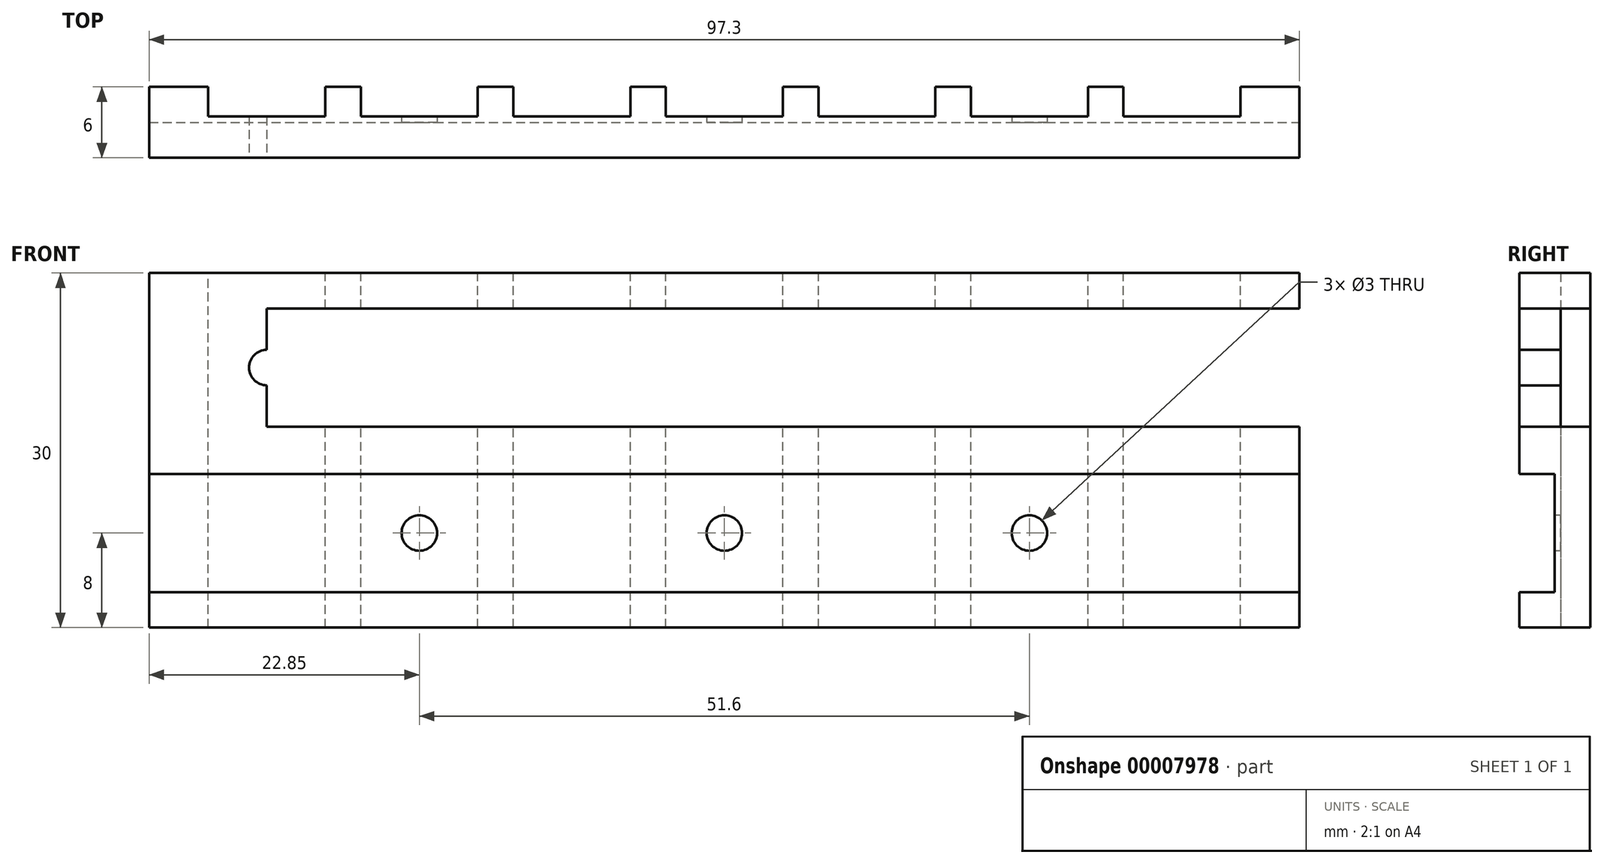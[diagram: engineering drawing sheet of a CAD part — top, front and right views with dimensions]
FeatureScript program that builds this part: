
annotation { "Feature Type Name" : "Feature", "Feature Type Description" : "" }
export const myFeature = defineFeature(function(context is Context, id is Id, definition is map)
    precondition{}
    {
        {
            var Q0;
            Q0=qCreatedBy(makeId("Front.planeOp"),FACE);
            var sketch = newSketch(context, id + "F0", { "sketchPlane" : qUnion([Q0])});
            skLineSegment(sketch, "E0.bottom", {"start": v(0, 0) * mm, "end": v(97.3, 0) * mm});
            skLineSegment(sketch, "E0.top", {"start": v(0, 30) * mm, "end": v(97.3, 30) * mm});
            skLineSegment(sketch, "E0.left", {"start": v(0, 0) * mm, "end": v(0, 30) * mm});
            skLineSegment(sketch, "E0.right", {"start": v(97.3, 0) * mm, "end": v(97.3, 30) * mm});
            skLineSegment(sketch, "E1.bottom", {"start": v(0, 27) * mm, "end": v(97.3, 27) * mm});
            skLineSegment(sketch, "E1.top", {"start": v(0, 17) * mm, "end": v(97.3, 17) * mm});
            skLineSegment(sketch, "E1.left", {"start": v(0, 27) * mm, "end": v(0, 17) * mm});
            skLineSegment(sketch, "E1.right", {"start": v(97.3, 27) * mm, "end": v(97.3, 17) * mm});
            skLineSegment(sketch, "E2.bottom", {"start": v(0, 13) * mm, "end": v(97.3, 13) * mm});
            skLineSegment(sketch, "E2.top", {"start": v(0, 3) * mm, "end": v(97.3, 3) * mm});
            skLineSegment(sketch, "E2.left", {"start": v(0, 13) * mm, "end": v(0, 3) * mm});
            skLineSegment(sketch, "E2.right", {"start": v(97.3, 13) * mm, "end": v(97.3, 3) * mm});
            skPoint(sketch, "E3.1", {"position": v(9.95, 0) * mm});
            skLineSegment(sketch, "E4", {"start": v(9.95, 0) * mm, "end": v(9.95, 30) * mm, "construction": true});
            skLineSegment(sketch, "E5", {"start": v(9.95, 27) * mm, "end": v(9.95, 17) * mm});
            skPoint(sketch, "E6", {"position": v(9.95, 22) * mm});
            skCircle(sketch, "E7", {"center": v(9.95, 22) * mm, "radius": 1.5 * mm});
            skCircle(sketch, "E8.1.0.0", {"center": v(35.75, 22) * mm, "radius": 1.5 * mm});
            skCircle(sketch, "E8.2.0.0", {"center": v(61.55, 22) * mm, "radius": 1.5 * mm});
            skCircle(sketch, "E8.3.0.0", {"center": v(87.35, 22) * mm, "radius": 1.5 * mm});
            skLineSegment(sketch, "E8.direction1", {"start": v(9.95, 22) * mm, "end": v(35.75, 22) * mm, "construction": true});
            skLineSegment(sketch, "E9.1.0.0", {"start": v(22.85, 0) * mm, "end": v(22.85, 30) * mm, "construction": true});
            skLineSegment(sketch, "E9.2.0.0", {"start": v(35.75, 0) * mm, "end": v(35.75, 30) * mm, "construction": true});
            skLineSegment(sketch, "E9.3.0.0", {"start": v(48.65, 0) * mm, "end": v(48.65, 30) * mm, "construction": true});
            skLineSegment(sketch, "E9.4.0.0", {"start": v(61.55, 0) * mm, "end": v(61.55, 30) * mm, "construction": true});
            skLineSegment(sketch, "E9.5.0.0", {"start": v(74.45, 0) * mm, "end": v(74.45, 30) * mm, "construction": true});
            skLineSegment(sketch, "E9.6.0.0", {"start": v(87.35, 0) * mm, "end": v(87.35, 30) * mm, "construction": true});
            skLineSegment(sketch, "E9.direction1", {"start": v(9.95, 0) * mm, "end": v(22.85, 0) * mm, "construction": true});
            skPoint(sketch, "E10", {"position": v(9.95, 8) * mm});
            skPoint(sketch, "E10.positionSnap0", {"position": v(0, 8) * mm});
            skLineSegment(sketch, "E11", {"start": v(0, 8) * mm, "end": v(97.3, 8) * mm, "construction": true});
            skCircle(sketch, "E12", {"center": v(22.85, 8) * mm, "radius": 1.5 * mm});
            skCircle(sketch, "E13.1.0.0", {"center": v(48.65, 8) * mm, "radius": 1.5 * mm});
            skCircle(sketch, "E13.2.0.0", {"center": v(74.45, 8) * mm, "radius": 1.5 * mm});
            skLineSegment(sketch, "E13.direction1", {"start": v(22.85, 8) * mm, "end": v(48.65, 8) * mm, "construction": true});
            skSolve(sketch);
        }
        {
            var Q0;
            Q0=makeQuery(id+"F0.imprint","IMPRINT",FACE,{"disambiguationData":[TD([[makeQuery(id+"F0.imprint","IMPRINT",EDGE,{"derivedFrom":sQuery(id+"F0.wireOp",EDGE,"E1.bottom")}),-1.0]])]});
            var Q1;
            {var subQ0=sQuery(id+"F0.wireOp",EDGE,"E1.top");Q1=makeQuery(id+"F0.imprint","IMPRINT",FACE,{"disambiguationData":[TD([[makeQuery(id+"F0.imprint","IMPRINT",EDGE,{"derivedFrom":subQ0}),-1.0]])]});}
            var Q2;
            Q2=makeQuery(id+"F0.imprint","IMPRINT",FACE,{"disambiguationData":[TD([[makeQuery(id+"F0.imprint","IMPRINT",EDGE,{"derivedFrom":sQuery(id+"F0.wireOp",EDGE,"E2.bottom")}),-1.0]])]});
            var Q3;
            {var subQ0=sQuery(id+"F0.wireOp",EDGE,"E0.bottom");Q3=makeQuery(id+"F0.imprint","IMPRINT",FACE,{"disambiguationData":[TD([[makeQuery(id+"F0.imprint","IMPRINT",EDGE,{"derivedFrom":subQ0}),1.0]])]});}
            var Q4;
            {var subQ8=sQuery(id+"F0.wireOp",EDGE,"E2.bottom");Q4=makeQuery(id+"F0.imprint","IMPRINT",FACE,{"disambiguationData":[TD([[makeQuery(id+"F0.imprint","IMPRINT",EDGE,{"derivedFrom":subQ8}),1.0]])]});}
            var Q5;
            {var subQ0=sQuery(id+"F0.wireOp",EDGE,"E1.bottom");var subQ1=makeQuery(id+"F0.imprint","INTERSECT",VERTEX,{"derivedFrom":[subQ0,sQuery(id+"F0.wireOp",EDGE,"E5")]});Q5=makeQuery(id+"F0.imprint","IMPRINT",FACE,{"disambiguationData":[TD([[makeQuery(id+"F0.imprint","IMPRINT",EDGE,{"disambiguationData":[TD([[subQ1,1.0]])],"derivedFrom":subQ0}),1.0]])]});}
            var Q6;
            {var subQ0=sQuery(id+"F0.wireOp",EDGE,"E1.top");var subQ1=makeQuery(id+"F0.imprint","INTERSECT",VERTEX,{"derivedFrom":[subQ0,sQuery(id+"F0.wireOp",EDGE,"E5")]});Q6=makeQuery(id+"F0.imprint","IMPRINT",FACE,{"disambiguationData":[TD([[makeQuery(id+"F0.imprint","IMPRINT",EDGE,{"disambiguationData":[TD([[subQ1,1.0]])],"derivedFrom":subQ0}),-1.0]])]});}
            var Q7;
            {var subQ0=sQuery(id+"F0.wireOp",EDGE,"E8.1.0.0");var subQ1=sQuery(id+"F0.wireOp",EDGE,"E1.top");var subQ2=makeQuery(id+"F0.imprint","INTERSECT",VERTEX,{"disambiguationData":[OD(0.0)],"derivedFrom":[subQ1,subQ0]});Q7=makeQuery(id+"F0.imprint","IMPRINT",FACE,{"disambiguationData":[TD([[makeQuery(id+"F0.imprint","IMPRINT",EDGE,{"disambiguationData":[TD([[subQ2,-1.0]])],"derivedFrom":subQ1}),-1.0]])]});}
            var Q8;
            {var subQ0=sQuery(id+"F0.wireOp",EDGE,"E8.2.0.0");var subQ1=sQuery(id+"F0.wireOp",EDGE,"E1.top");var subQ2=makeQuery(id+"F0.imprint","INTERSECT",VERTEX,{"disambiguationData":[OD(0.0)],"derivedFrom":[subQ1,subQ0]});Q8=makeQuery(id+"F0.imprint","IMPRINT",FACE,{"disambiguationData":[TD([[makeQuery(id+"F0.imprint","IMPRINT",EDGE,{"disambiguationData":[TD([[subQ2,-1.0]])],"derivedFrom":subQ1}),-1.0]])]});}
            var Q9;
            {var subQ0=sQuery(id+"F0.wireOp",EDGE,"E8.3.0.0");var subQ1=sQuery(id+"F0.wireOp",EDGE,"E1.top");var subQ2=makeQuery(id+"F0.imprint","INTERSECT",VERTEX,{"disambiguationData":[OD(0.0)],"derivedFrom":[subQ1,subQ0]});Q9=makeQuery(id+"F0.imprint","IMPRINT",FACE,{"disambiguationData":[TD([[makeQuery(id+"F0.imprint","IMPRINT",EDGE,{"disambiguationData":[TD([[subQ2,-1.0]])],"derivedFrom":subQ1}),-1.0]])]});}
            var Q10;
            {var subQ17=sQuery(id+"F0.wireOp",EDGE,"E0.top");Q10=makeQuery(id+"F0.imprint","IMPRINT",FACE,{"disambiguationData":[TD([[makeQuery(id+"F0.imprint","IMPRINT",EDGE,{"derivedFrom":subQ17}),-1.0]])]});}
            var Q11;
            {var subQ0=sQuery(id+"F0.wireOp",EDGE,"E8.1.0.0");var subQ1=sQuery(id+"F0.wireOp",EDGE,"E1.bottom");var subQ2=makeQuery(id+"F0.imprint","INTERSECT",VERTEX,{"disambiguationData":[OD(0.0)],"derivedFrom":[subQ1,subQ0]});Q11=makeQuery(id+"F0.imprint","IMPRINT",FACE,{"disambiguationData":[TD([[makeQuery(id+"F0.imprint","IMPRINT",EDGE,{"disambiguationData":[TD([[subQ2,-1.0]])],"derivedFrom":subQ1}),1.0]])]});}
            var Q12;
            {var subQ0=sQuery(id+"F0.wireOp",EDGE,"E8.2.0.0");var subQ1=sQuery(id+"F0.wireOp",EDGE,"E1.bottom");var subQ2=makeQuery(id+"F0.imprint","INTERSECT",VERTEX,{"disambiguationData":[OD(0.0)],"derivedFrom":[subQ1,subQ0]});Q12=makeQuery(id+"F0.imprint","IMPRINT",FACE,{"disambiguationData":[TD([[makeQuery(id+"F0.imprint","IMPRINT",EDGE,{"disambiguationData":[TD([[subQ2,-1.0]])],"derivedFrom":subQ1}),1.0]])]});}
            var Q13;
            {var subQ0=sQuery(id+"F0.wireOp",EDGE,"E8.3.0.0");var subQ1=sQuery(id+"F0.wireOp",EDGE,"E1.bottom");var subQ2=makeQuery(id+"F0.imprint","INTERSECT",VERTEX,{"disambiguationData":[OD(0.0)],"derivedFrom":[subQ1,subQ0]});Q13=makeQuery(id+"F0.imprint","IMPRINT",FACE,{"disambiguationData":[TD([[makeQuery(id+"F0.imprint","IMPRINT",EDGE,{"disambiguationData":[TD([[subQ2,-1.0]])],"derivedFrom":subQ1}),1.0]])]});}
            var Q14;
            {var subQ5=sQuery(id+"F0.wireOp",EDGE,"E1.right");Q14=makeQuery(id+"F0.imprint","IMPRINT",FACE,{"disambiguationData":[TD([[makeQuery(id+"F0.imprint","IMPRINT",EDGE,{"derivedFrom":subQ5}),-1.0]])]});}
            extrude(context, id + "F1", {"entities" : qUnion([Q0, Q1, Q2, Q3, Q4, Q5, Q6, Q7, Q8, Q9, Q10, Q11, Q12, Q13, Q14]), "oppositeDirection" : true, "depth" : 6 * mm});
        }
        {
            var Q0;
            Q0=qCreatedBy(makeId("Top.planeOp"),FACE);
            var sketch = newSketch(context, id + "F2", { "sketchPlane" : qUnion([Q0])});
            skLineSegment(sketch, "E14.bottom", {"start": v(5, 13.4) * mm, "end": v(14.9, 13.4) * mm});
            skLineSegment(sketch, "E14.top", {"start": v(5, 3.5) * mm, "end": v(14.9, 3.5) * mm});
            skLineSegment(sketch, "E14.left", {"start": v(5, 13.4) * mm, "end": v(5, 3.5) * mm});
            skLineSegment(sketch, "E14.right", {"start": v(14.9, 13.4) * mm, "end": v(14.9, 3.5) * mm});
            skLineSegment(sketch, "E15.1.0.0", {"start": v(27.8, 13.4) * mm, "end": v(27.8, 3.5) * mm});
            skLineSegment(sketch, "E15.1.0.1", {"start": v(17.9, 3.5) * mm, "end": v(27.8, 3.5) * mm});
            skLineSegment(sketch, "E15.1.0.2", {"start": v(17.9, 13.4) * mm, "end": v(17.9, 3.5) * mm});
            skLineSegment(sketch, "E15.1.0.3", {"start": v(17.9, 13.4) * mm, "end": v(27.8, 13.4) * mm});
            skLineSegment(sketch, "E15.2.0.0", {"start": v(40.7, 13.4) * mm, "end": v(40.7, 3.5) * mm});
            skLineSegment(sketch, "E15.2.0.1", {"start": v(30.8, 3.5) * mm, "end": v(40.7, 3.5) * mm});
            skLineSegment(sketch, "E15.2.0.2", {"start": v(30.8, 13.4) * mm, "end": v(30.8, 3.5) * mm});
            skLineSegment(sketch, "E15.2.0.3", {"start": v(30.8, 13.4) * mm, "end": v(40.7, 13.4) * mm});
            skLineSegment(sketch, "E15.3.0.0", {"start": v(53.6, 13.4) * mm, "end": v(53.6, 3.5) * mm});
            skLineSegment(sketch, "E15.3.0.1", {"start": v(43.7, 3.5) * mm, "end": v(53.6, 3.5) * mm});
            skLineSegment(sketch, "E15.3.0.2", {"start": v(43.7, 13.4) * mm, "end": v(43.7, 3.5) * mm});
            skLineSegment(sketch, "E15.3.0.3", {"start": v(43.7, 13.4) * mm, "end": v(53.6, 13.4) * mm});
            skLineSegment(sketch, "E15.4.0.0", {"start": v(66.5, 13.4) * mm, "end": v(66.5, 3.5) * mm});
            skLineSegment(sketch, "E15.4.0.1", {"start": v(56.6, 3.5) * mm, "end": v(66.5, 3.5) * mm});
            skLineSegment(sketch, "E15.4.0.2", {"start": v(56.6, 13.4) * mm, "end": v(56.6, 3.5) * mm});
            skLineSegment(sketch, "E15.4.0.3", {"start": v(56.6, 13.4) * mm, "end": v(66.5, 13.4) * mm});
            skLineSegment(sketch, "E15.5.0.0", {"start": v(79.4, 13.4) * mm, "end": v(79.4, 3.5) * mm});
            skLineSegment(sketch, "E15.5.0.1", {"start": v(69.5, 3.5) * mm, "end": v(79.4, 3.5) * mm});
            skLineSegment(sketch, "E15.5.0.2", {"start": v(69.5, 13.4) * mm, "end": v(69.5, 3.5) * mm});
            skLineSegment(sketch, "E15.5.0.3", {"start": v(69.5, 13.4) * mm, "end": v(79.4, 13.4) * mm});
            skLineSegment(sketch, "E15.6.0.0", {"start": v(92.3, 13.4) * mm, "end": v(92.3, 3.5) * mm});
            skLineSegment(sketch, "E15.6.0.1", {"start": v(82.4, 3.5) * mm, "end": v(92.3, 3.5) * mm});
            skLineSegment(sketch, "E15.6.0.2", {"start": v(82.4, 13.4) * mm, "end": v(82.4, 3.5) * mm});
            skLineSegment(sketch, "E15.6.0.3", {"start": v(82.4, 13.4) * mm, "end": v(92.3, 13.4) * mm});
            skLineSegment(sketch, "E15.direction1", {"start": v(14.9, 3.5) * mm, "end": v(27.8, 3.5) * mm, "construction": true});
            skPoint(sketch, "E16", {"position": v(9.95, 3.5) * mm});
            skPoint(sketch, "E17", {"position": v(22.85, 3.5) * mm});
            skPoint(sketch, "E18", {"position": v(35.75, 3.5) * mm});
            skPoint(sketch, "E19", {"position": v(48.65, 3.5) * mm});
            skPoint(sketch, "E20", {"position": v(61.55, 3.5) * mm});
            skPoint(sketch, "E21", {"position": v(74.45, 3.5) * mm});
            skPoint(sketch, "E22", {"position": v(87.35, 3.5) * mm});
            skSolve(sketch);
        }
        {
            var Q0;
            Q0=makeQuery(id+"F2.imprint","IMPRINT",FACE,{"disambiguationData":[TD([[makeQuery(id+"F2.imprint","IMPRINT",EDGE,{"derivedFrom":sQuery(id+"F2.wireOp",EDGE,"E14.bottom")}),-1.0]])]});
            var Q1;
            Q1=makeQuery(id+"F2.imprint","IMPRINT",FACE,{"disambiguationData":[TD([[makeQuery(id+"F2.imprint","IMPRINT",EDGE,{"derivedFrom":sQuery(id+"F2.wireOp",EDGE,"E15.1.0.0")}),-1.0]])]});
            var Q2;
            Q2=makeQuery(id+"F2.imprint","IMPRINT",FACE,{"disambiguationData":[TD([[makeQuery(id+"F2.imprint","IMPRINT",EDGE,{"derivedFrom":sQuery(id+"F2.wireOp",EDGE,"E15.2.0.0")}),-1.0]])]});
            var Q3;
            Q3=makeQuery(id+"F2.imprint","IMPRINT",FACE,{"disambiguationData":[TD([[makeQuery(id+"F2.imprint","IMPRINT",EDGE,{"derivedFrom":sQuery(id+"F2.wireOp",EDGE,"E15.3.0.0")}),-1.0]])]});
            var Q4;
            Q4=makeQuery(id+"F2.imprint","IMPRINT",FACE,{"disambiguationData":[TD([[makeQuery(id+"F2.imprint","IMPRINT",EDGE,{"derivedFrom":sQuery(id+"F2.wireOp",EDGE,"E15.4.0.0")}),-1.0]])]});
            var Q5;
            Q5=makeQuery(id+"F2.imprint","IMPRINT",FACE,{"disambiguationData":[TD([[makeQuery(id+"F2.imprint","IMPRINT",EDGE,{"derivedFrom":sQuery(id+"F2.wireOp",EDGE,"E15.5.0.0")}),-1.0]])]});
            var Q6;
            Q6=makeQuery(id+"F2.imprint","IMPRINT",FACE,{"disambiguationData":[TD([[makeQuery(id+"F2.imprint","IMPRINT",EDGE,{"derivedFrom":sQuery(id+"F2.wireOp",EDGE,"E15.6.0.0")}),-1.0]])]});
            extrude(context, id + "F3", {"entities" : qUnion([Q0, Q1, Q2, Q3, Q4, Q5, Q6]), "operationType" : NewBodyOperationType.REMOVE, "endBound" : BoundingType.THROUGH_ALL, "depth" : 10 * mm});
        }
        {
            var Q0;
            {var subQ5=sQuery(id+"F0.wireOp",EDGE,"E1.left");Q0=makeQuery(id+"F0.imprint","IMPRINT",FACE,{"disambiguationData":[TD([[makeQuery(id+"F0.imprint","IMPRINT",EDGE,{"derivedFrom":subQ5}),1.0]])]});}
            var Q1;
            {var subQ5=sQuery(id+"F0.wireOp",EDGE,"E1.right");Q1=makeQuery(id+"F0.imprint","IMPRINT",FACE,{"disambiguationData":[TD([[makeQuery(id+"F0.imprint","IMPRINT",EDGE,{"derivedFrom":subQ5}),-1.0]])]});}
            var Q2;
            Q2=makeQuery(id+"F0.imprint","IMPRINT",FACE,{"disambiguationData":[TD([[makeQuery(id+"F0.imprint","IMPRINT",EDGE,{"derivedFrom":sQuery(id+"F0.wireOp",EDGE,"E2.bottom")}),-1.0]])]});
            extrude(context, id + "F4", {"entities" : qUnion([Q0, Q1, Q2]), "operationType" : NewBodyOperationType.REMOVE, "oppositeDirection" : true, "depth" : 3 * mm});
        }
    });
